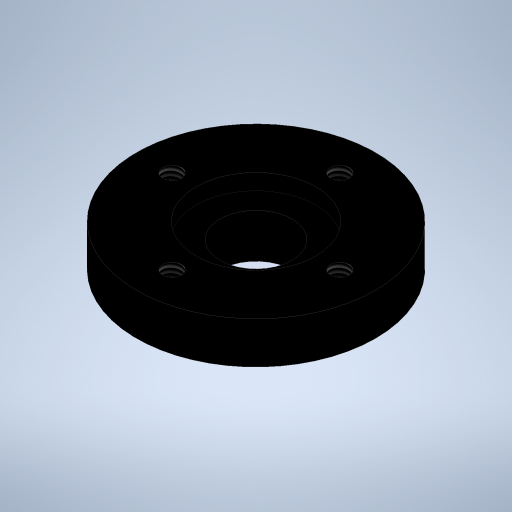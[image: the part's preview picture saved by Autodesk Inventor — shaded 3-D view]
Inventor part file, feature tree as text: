
AUTODESK INVENTOR PART (.ipt)
format: ipt  version: 2024.1 (Build 281209000, 209)  size: 273,920 bytes
history: native  units: mm
features: sketch x2, other x1, revolve x1, hole x1
ambient origin geometry x8: Origin, YZ Plane, XZ Plane, XY Plane, X Axis, Y Axis, Z Axis, Center Point
bodies: Body1 (feature_tree)
feature tree (5):
  other  "솔리드1"
  revolve  "회전1"
  hole  "Hole2"  [1 undecoded]
  sketch  "스케치1"
  sketch  "Sketch3"  dims[d5=360.0deg d22=6.0mm d23=8.96mm d24=10.0mm d25=19.92mm d26=1.32mm d27=5.0mm d28=3.48mm d29=7.0mm d30=40.0mm d32=360.0deg d34=1.567mm d35=3.48mm d36=4.0mm d37=2.0mm d38=90.0deg d39=8.0mm d40=20.594885mm]
note: 1 required parameter value undecoded (feature->parameter linkage not recoverable at this tier; creation-order binding heuristic only, values carry confidence <= 0.55)
